# Revit family: Edge F Corner
name_source: partatom
category: Windows
units: mm (PartAtom-declared; Revit-internal decimal feet)

## family parameters
Always vertical = Yes
Cut with Voids When Loaded = No
Host = Wall
OmniClass Number = 23.30.20.00
OmniClass Title = Windows
Room Calculation Point = No
Shared = No

## types (2) — shared parameters
Analytic Construction = <None>
Default Sill Height = 1' - 0"
Fin Center Line = 0' - 0 1/2"
Jamb Offset = 0' - 1 1/2"
Panel Offset = 0' - 2 11/32"
Wall Closure = By host

## per-type parameters (varying)
| type | Fin At Jamb | Fin At Jamb 2 | Height | Jamb | Jamb 2 | NFW | NFW 2 | Panel Length | Panel Length 2 | Width | Width 2 | Width 2 Fin Void (If Needed) | Width Fin Void (If Needed) |
| OVO (JAMBS) | No | No | 7' - 0" | Yes | Yes | 3' - 3 27/32" | 1' - 9 27/32" | 3' - 1" | 1' - 7" | 3' - 0" | 1' - 6" | 0' - 0 1/32" | 0' - 0 1/32" |
| OVO (FINS AT JAMBS) | Yes | Yes | 8' - 0" | No | No | 4' - 3 27/32" | 4' - 3 27/32" | 4' - 1" | 4' - 1" | 4' - 0" | 4' - 0" | 0' - 1 5/8" | 0' - 1 5/8" |

## geometry (parser evidence)
native form markers: Sweep x19
no freeform markers — native parametric forms only
